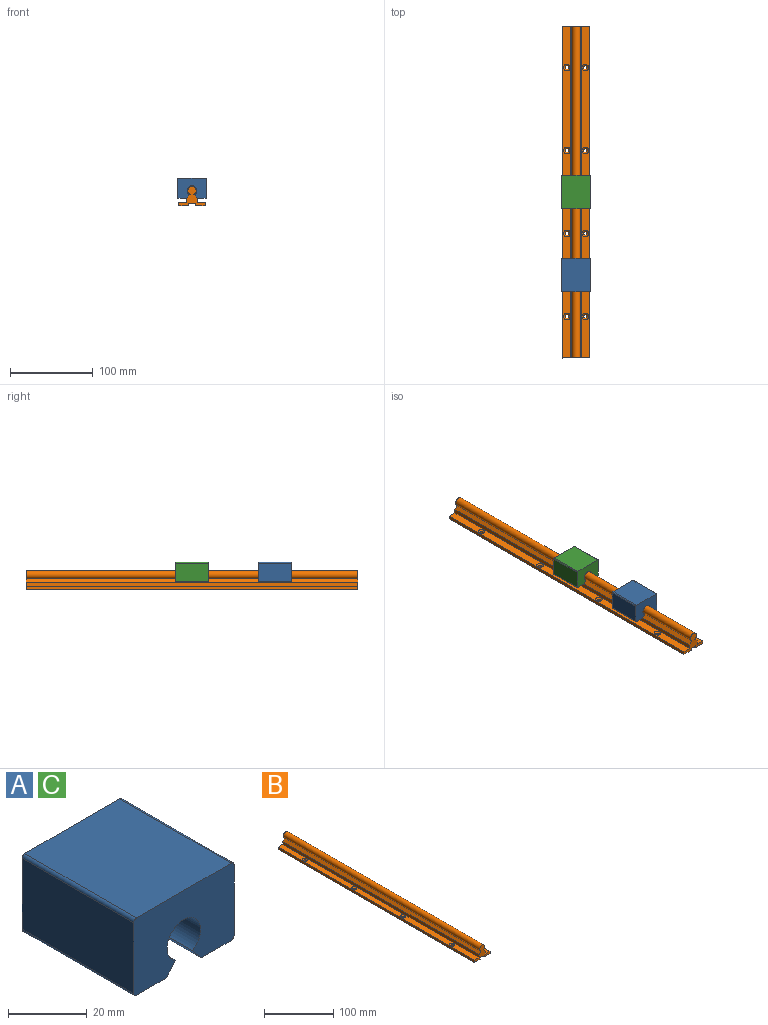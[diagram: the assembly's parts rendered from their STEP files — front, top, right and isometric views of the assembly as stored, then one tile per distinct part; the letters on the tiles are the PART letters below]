
ASSEMBLY  parts=3 mates=2
PART A: 16 faces, bbox 36x40x24 mm
  f0: plane 40x22mm, normal (-1,0,0), area 880mm2, adj f1,f13,f14,f15
  f1: cylinder r=1mm len=40mm, axis (0,1,0), area 62.8mm2, adj f0,f2,f14,f15
  f2: plane 40x10.34mm, normal (0,0,-1), area 413.7mm2, adj f1,f3,f14,f15
  f3: cylinder r=1mm len=40mm, axis (0,1,0), area 34.9mm2, adj f2,f4,f14,f15
  f4: plane 40x3.45mm, normal (0.77,0,-0.64), area 180mm2, adj f3,f5,f14,f15
  f5: cylinder r=6mm len=40mm, axis (0,1,0), area 1256.6mm2, adj f4,f6,f14,f15
  f6: plane 40x3.45mm, normal (-0.77,0,-0.64), area 180mm2, adj f5,f7,f14,f15
  f7: cylinder r=1mm len=40mm, axis (0,1,0), area 34.9mm2, adj f6,f8,f14,f15
  f8: plane 40x10.34mm, normal (0,0,-1), area 413.7mm2, adj f7,f9,f14,f15
  f9: cylinder r=1mm len=40mm, axis (0,1,0), area 62.8mm2, adj f8,f10,f14,f15
  f10: plane 40x22mm, normal (1,0,0), area 880mm2, adj f9,f11,f14,f15
  f11: cylinder r=1mm len=40mm, axis (0,1,0), area 62.8mm2, adj f10,f12,f14,f15
  f12: plane 40x34mm, normal (0,0,1), area 1360mm2, adj f11,f13,f14,f15
  f13: cylinder r=1mm len=40mm, axis (0,1,0), area 62.8mm2, adj f0,f12,f14,f15
  f14: plane 36x24mm, normal (0,-1,0), area 718.3mm2, adj f0,f1,f2,f3,f4,f5,f6,f7
  f15: plane 36x24mm, normal (0,1,0), area 718.3mm2, adj f0,f1,f2,f3,f4,f5,f6,f7
PART B: 32 faces, bbox 32x400x23 mm
  f0: plane 32x23mm, normal (0,-1,0), area 281.5mm2, adj f1,f2,f3,f4,f5,f6,f7,f8
  f1: plane 400x9.8mm, normal (0,0,1), area 3718.9mm2, adj f0,f2,f14,f15,f17,f23,f25,f29
  f2: plane 400x4.9mm, normal (1,0,0), area 1960mm2, adj f0,f1,f3,f15
  f3: plane 400x4.69mm, normal (0.77,0,0.63), area 2426.1mm2, adj f0,f2,f4,f15
  f4: cylinder r=5mm len=400mm, axis (0,1,0), area 10609.2mm2, adj f0,f3,f5,f15
  f5: plane 400x4.69mm, normal (-0.77,0,0.63), area 2426.1mm2, adj f0,f4,f6,f15
  f6: plane 400x4.9mm, normal (-1,0,0), area 1960mm2, adj f0,f5,f7,f15
  f7: plane 400x9.8mm, normal (0,0,1), area 3718.9mm2, adj f0,f6,f8,f15,f19,f21,f27,f31
  f8: plane 400x4mm, normal (-1,0,0), area 1600mm2, adj f0,f7,f9,f15
  f9: plane 400x12mm, normal (0,0,-1), area 4736.4mm2, adj f0,f8,f10,f15,f18,f20,f26,f30
  f10: plane 400x3mm, normal (1,0,0), area 1200mm2, adj f0,f9,f11,f15
  f11: plane 400x8mm, normal (0,0,-1), area 3200mm2, adj f0,f10,f12,f15
  f12: plane 400x3mm, normal (-1,0,0), area 1200mm2, adj f0,f11,f13,f15
  f13: plane 400x12mm, normal (0,0,-1), area 4736.4mm2, adj f0,f12,f14,f15,f16,f22,f24,f28
  f14: plane 400x4mm, normal (1,0,0), area 1600mm2, adj f0,f1,f13,f15
  f15: plane 32x23mm, normal (0,1,0), area 281.5mm2, adj f1,f2,f3,f4,f5,f6,f7,f8
  f16: cylinder r=2.25mm len=4.5mm, axis (0,0,1), area 31.8mm2, adj f13,f17
  f17: cone r=2.25mm half-angle=45deg, axis (0,0,1), area 48.6mm2, adj f1,f16
  f18: cylinder r=2.25mm len=4.5mm, axis (0,0,1), area 31.8mm2, adj f9,f19
  f19: cone r=2.25mm half-angle=45deg, axis (0,0,1), area 48.6mm2, adj f7,f18
  f20: cylinder r=2.25mm len=4.5mm, axis (0,0,1), area 31.8mm2, adj f9,f21
  f21: cone r=2.25mm half-angle=45deg, axis (0,0,1), area 48.6mm2, adj f7,f20
  f22: cylinder r=2.25mm len=4.5mm, axis (0,0,1), area 31.8mm2, adj f13,f23
  f23: cone r=2.25mm half-angle=45deg, axis (0,0,1), area 48.6mm2, adj f1,f22
  f24: cylinder r=2.25mm len=4.5mm, axis (0,0,1), area 31.8mm2, adj f13,f25
  f25: cone r=2.25mm half-angle=45deg, axis (0,0,1), area 48.6mm2, adj f1,f24
  f26: cylinder r=2.25mm len=4.5mm, axis (0,0,1), area 31.8mm2, adj f9,f27
  f27: cone r=2.25mm half-angle=45deg, axis (0,0,1), area 48.6mm2, adj f7,f26
  f28: cylinder r=2.25mm len=4.5mm, axis (0,0,1), area 31.8mm2, adj f13,f29
  f29: cone r=2.25mm half-angle=45deg, axis (0,0,1), area 48.6mm2, adj f1,f28
  f30: cylinder r=2.25mm len=4.5mm, axis (0,0,1), area 31.8mm2, adj f9,f31
  f31: cone r=2.25mm half-angle=45deg, axis (0,0,1), area 48.6mm2, adj f7,f30
PART C: same geometry as A
PLACE A rot(axis=(0.19,-0.32,0.93),0deg) t=(3.97,-92.82,22)mm
PLACE B rot(axis=(0.19,-0.32,0.93),0deg) t=(3.97,187.18,9.19)mm
PLACE C rot(axis=(0.19,-0.32,0.93),0deg) t=(3.97,7.18,22)mm
MATE slider C.f5 <-> B.f4  axis (0,1,0) through (3.97,-12.82,27.19)mm
MATE slider A.f5 <-> B.f4  axis (0,1,0) through (3.97,-112.82,27.19)mm
